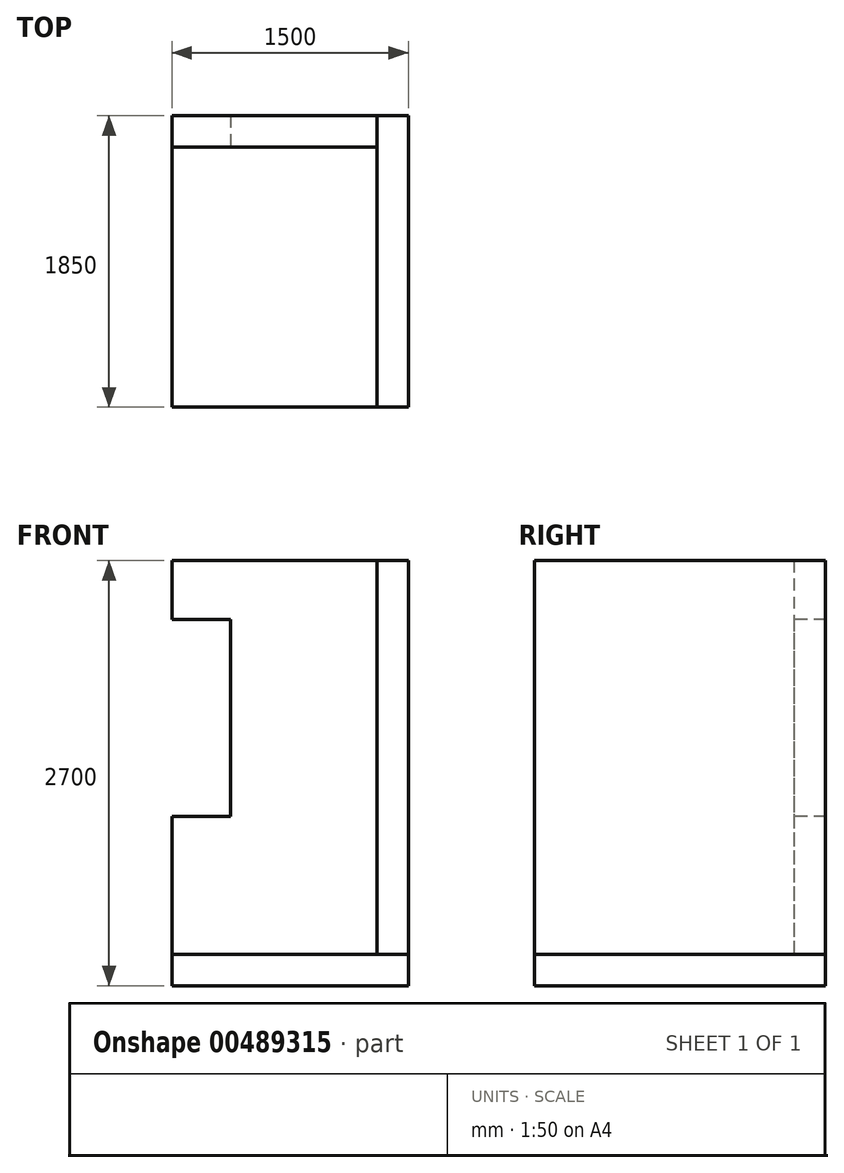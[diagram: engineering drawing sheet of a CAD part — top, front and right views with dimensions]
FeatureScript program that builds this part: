
annotation { "Feature Type Name" : "Feature", "Feature Type Description" : "" }
export const myFeature = defineFeature(function(context is Context, id is Id, definition is map)
    precondition{}
    {
        {
            var Q0;
            Q0=qCreatedBy(makeId("Top.planeOp"),FACE);
            var sketch = newSketch(context, id + "F0", { "sketchPlane" : qUnion([Q0])});
            skLineSegment(sketch, "E0.bottom", {"start": v(0, 0) * mm, "end": v(-1500, 0) * mm});
            skLineSegment(sketch, "E0.top", {"start": v(0, -1850) * mm, "end": v(-1500, -1850) * mm});
            skLineSegment(sketch, "E0.left", {"start": v(0, 0) * mm, "end": v(0, -1850) * mm});
            skLineSegment(sketch, "E0.right", {"start": v(-1500, 0) * mm, "end": v(-1500, -1850) * mm});
            skSolve(sketch);
        }
        {
            var Q0;
            Q0 = qSketchRegion(id + "F0", true);
            extrude(context, id + "F1", {"entities" : qUnion([Q0]), "depth" : -200 * mm});
        }
        {
            var Q0;
            Q0=makeQuery(id+"F1.opExtrude","CAP_FACE",FACE,{"disambiguationData":[OSD([sQuery(id+"F0.wireOp",EDGE,"E0.bottom"),sQuery(id+"F0.wireOp",EDGE,"E0.top"),sQuery(id+"F0.wireOp",EDGE,"E0.left"),sQuery(id+"F0.wireOp",EDGE,"E0.right")])],"isStart":true});
            var sketch = newSketch(context, id + "F2", { "sketchPlane" : qUnion([Q0])});
            skLineSegment(sketch, "E1.bottom", {"start": v(-1500, 0) * mm, "end": v(0, 0) * mm});
            skLineSegment(sketch, "E1.top", {"start": v(-1500, -200) * mm, "end": v(-200, -200) * mm});
            skLineSegment(sketch, "E1.left", {"start": v(-1500, 0) * mm, "end": v(-1500, -200) * mm});
            skLineSegment(sketch, "E2.top", {"start": v(-200, -1850) * mm, "end": v(0, -1850) * mm});
            skLineSegment(sketch, "E2.left", {"start": v(-200, 0) * mm, "end": v(-200, -1850) * mm});
            skLineSegment(sketch, "E2.right", {"start": v(0, 0) * mm, "end": v(0, -1850) * mm});
            skSolve(sketch);
        }
        {
            var Q0;
            {var subQ4=sQuery(id+"F2.wireOp",EDGE,"E1.top");Q0=makeQuery(id+"F2.imprint","IMPRINT",FACE,{"disambiguationData":[TD([[makeQuery(id+"F2.imprint","IMPRINT",EDGE,{"derivedFrom":subQ4}),1.0]])]});}
            extrude(context, id + "F3", {"entities" : qUnion([Q0]), "depth" : 2500 * mm});
        }
        {
            var Q0;
            Q0=makeQuery(id+"F3.opExtrude","SWEPT_FACE",FACE,{"disambiguationData":[OSD([sQuery(id+"F2.wireOp",EDGE,"E1.top")])]});
            var sketch = newSketch(context, id + "F4", { "sketchPlane" : qUnion([Q0])});
            skLineSegment(sketch, "E3.bottom", {"start": v(-1500, 2125) * mm, "end": v(-1130, 2125) * mm});
            skLineSegment(sketch, "E3.top", {"start": v(-1500, 875) * mm, "end": v(-1130, 875) * mm});
            skLineSegment(sketch, "E3.left", {"start": v(-1500, 2125) * mm, "end": v(-1500, 875) * mm});
            skLineSegment(sketch, "E3.right", {"start": v(-1130, 2125) * mm, "end": v(-1130, 875) * mm});
            skSolve(sketch);
        }
        {
            var Q0;
            Q0 = qSketchRegion(id + "F4", true);
            var Q1;
            Q1=makeQuery(id+"F3.boolean.opBoolean","MERGE",FACE,{"derivedFrom":[makeQuery(id+"F1.opExtrude","SWEPT_FACE",FACE,{"disambiguationData":[OSD([sQuery(id+"F0.wireOp",EDGE,"E0.bottom")])]}),makeQuery(id+"F3.opExtrude","SWEPT_FACE",FACE,{"disambiguationData":[OSD([sQuery(id+"F2.wireOp",EDGE,"E1.bottom")])]})]});
            var Q2;
            Q2=makeQuery(id+"F3.boolean.opBoolean","MERGE",FACE,{"derivedFrom":[makeQuery(id+"F1.opExtrude","SWEPT_FACE",FACE,{"disambiguationData":[OSD([sQuery(id+"F0.wireOp",EDGE,"E0.bottom")])]}),makeQuery(id+"F3.opExtrude","SWEPT_FACE",FACE,{"disambiguationData":[OSD([sQuery(id+"F2.wireOp",EDGE,"E1.bottom")])]})]});
            extrude(context, id + "F5", {"entities" : qUnion([Q0, Q1]), "operationType" : NewBodyOperationType.REMOVE, "endBound" : BoundingType.THROUGH_ALL, "oppositeDirection" : true, "endBoundEntityFace" : qUnion([Q2]), "depth" : 25 * mm});
        }
        {
            var Q0;
            {var subQ2=sQuery(id+"F2.wireOp",EDGE,"E2.top");Q0=makeQuery(id+"F2.imprint","IMPRINT",FACE,{"disambiguationData":[TD([[makeQuery(id+"F2.imprint","IMPRINT",EDGE,{"derivedFrom":subQ2}),-1.0]])]});}
            var Q1;
            Q1=makeQuery(id+"F3.opExtrude","CAP_FACE",FACE,{"disambiguationData":[OSD([sQuery(id+"F2.wireOp",EDGE,"E1.bottom"),sQuery(id+"F2.wireOp",EDGE,"E1.top"),sQuery(id+"F2.wireOp",EDGE,"E1.left"),sQuery(id+"F2.wireOp",EDGE,"E2.left")])],"isStart":false});
            extrude(context, id + "F6", {"entities" : qUnion([Q0]), "endBound" : BoundingType.UP_TO_SURFACE, "endBoundEntityFace" : qUnion([Q1]), "depth" : 25 * mm});
        }
    });
